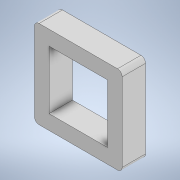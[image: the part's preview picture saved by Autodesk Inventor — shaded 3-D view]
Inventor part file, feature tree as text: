
AUTODESK INVENTOR PART (.ipt)
format: ipt  version: 2022.1 (Build 261234000, 234)  size: 107,520 bytes
history: native  units: in
note: dims shown in document units (in); Inventor stores cm internally (conversion verified against a paired STEP export)
features: extrude x2, sketch x2, fillet x1
ambient origin geometry x8: Origin, YZ Plane, XZ Plane, XY Plane, X Axis, Y Axis, Z Axis, Center Point
bodies: Solid1 (feature_tree)
feature tree (5):
  extrude  "Extrusion1"  Depth=0.6299in TaperAngle=0.0deg
  fillet  "Fillet1"  Radius=0.125in
  extrude  "Extrusion2"  Depth=0.6299in TaperAngle=0.0deg
  sketch  "Sketch1"  dims[d0=2.3622in d1=0.6299in d2=0.0in d3=0.125in]
  sketch  "Sketch2"  dims[d4=1.5748in d5=0.6299in d6=0.0in]
